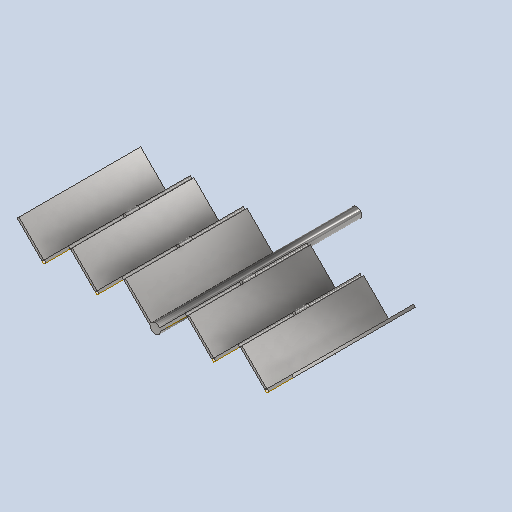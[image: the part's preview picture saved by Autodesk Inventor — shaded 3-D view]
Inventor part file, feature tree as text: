
AUTODESK INVENTOR PART (.ipt)
format: ipt  version: 2024 (Build 280153000, 153)  size: 287,744 bytes
history: native  units: in
note: dims shown in document units (in); Inventor stores cm internally (conversion verified against a paired STEP export)
features: other x13, plane x3
ambient origin geometry x8: Origin, YZ Plane, XZ Plane, XY Plane, X Axis, Y Axis, Z Axis, Center Point
bodies: Solid1 (feature_tree)
feature tree (16):
  other  "hubble_solar_panel.ipt"
  other  "Solid1::hubble_solar_panel.ipt"
  other  "TaggingFeature1"
  other  "pole_diameter_sketch"
  other  "pole_slot_diameter_sketch"
  other  "solar_panel_loft_guide_rear"
  other  "solar_panel_loft_guide_front"
  other  "solar_panel_hinge_cutout_sketch"
  other  "solar_panel_hinge_sketch"
  plane  "Work Plane1"
  plane  "Work Plane2"
  plane  "Work Plane3"
  other  "Srf1"
  other  "Srf2"
  other  "Srf2::Derived"
  other  "Srf4::Derived"
